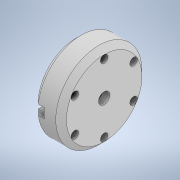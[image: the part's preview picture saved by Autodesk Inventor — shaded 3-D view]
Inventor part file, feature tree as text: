
AUTODESK INVENTOR PART (.ipt)
format: ipt  version: 2022 (Build 260153000, 153)  size: 167,424 bytes
history: native  units: mm
features: sketch x4, revolve x2, other x1, hole x1, extrude x1
ambient origin geometry x8: Origin, YZ Plane, XZ Plane, XY Plane, X Axis, Y Axis, Z Axis, Center Point
bodies: Body1 (feature_tree)
feature tree (9):
  other  "Твердое тело1"
  hole  "Отверстие1"  [1 undecoded]
  extrude  "Выдавливание1"  Depth=60.0mm TaperAngle=360.0deg
  sketch  "Эскиз3"
  sketch  "Эскиз4"
  revolve  "Вращение2"
  sketch  "Эскиз1"
  sketch  "Эскиз2"
  revolve  "Вращение1"
note: 1 required parameter value undecoded (feature->parameter linkage not recoverable at this tier; creation-order binding heuristic only, values carry confidence <= 0.55)
